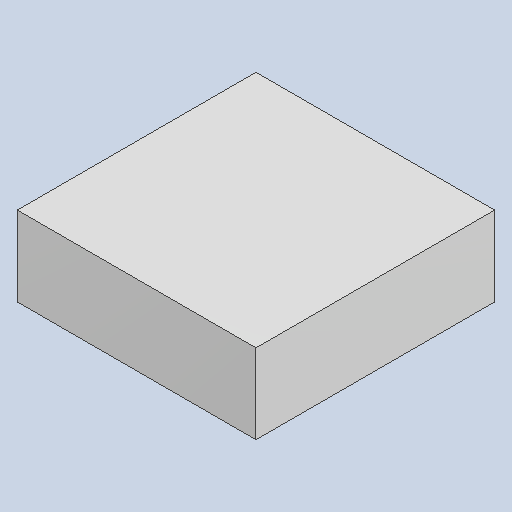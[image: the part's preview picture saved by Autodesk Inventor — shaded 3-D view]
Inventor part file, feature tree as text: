
AUTODESK INVENTOR PART (.ipt)
format: ipt  version: 2023.4 (Build 274418000, 418)  size: 79,872 bytes
history: native  units: mm
features: extrude x1
ambient origin geometry x8: Origin, YZ Plane, XZ Plane, XY Plane, X Axis, Y Axis, Z Axis, Center Point
bodies: Solid1 (feature_tree)
feature tree (1):
  extrude  "Extruded_56"  [1 undecoded]
note: 1 required parameter value undecoded (feature->parameter linkage not recoverable at this tier; creation-order binding heuristic only, values carry confidence <= 0.55)
